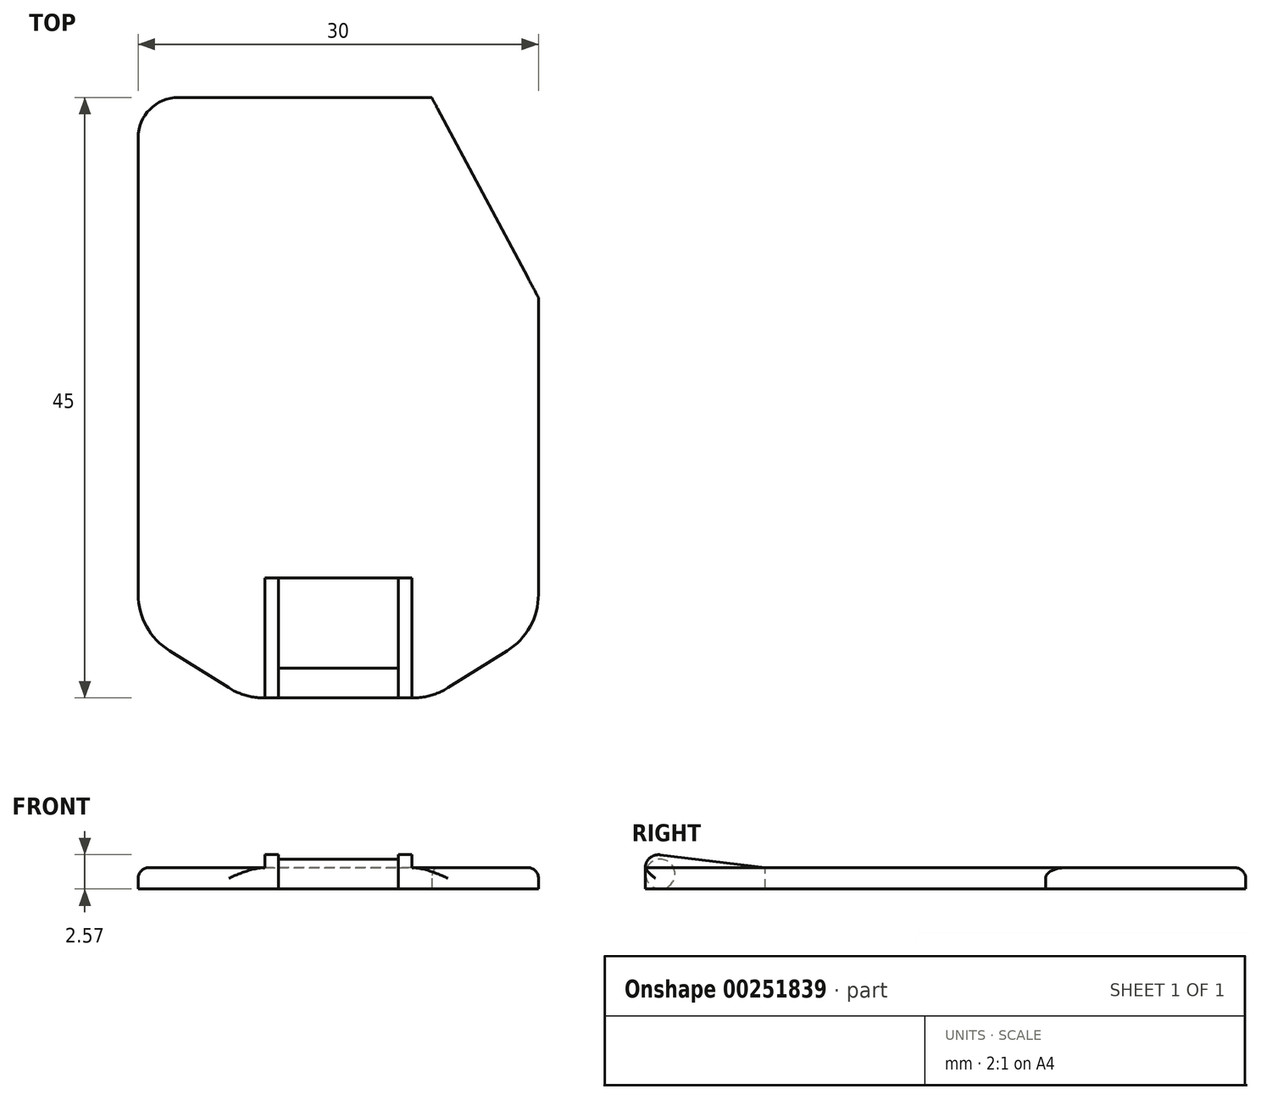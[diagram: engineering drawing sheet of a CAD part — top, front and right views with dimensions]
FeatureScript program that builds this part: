
annotation { "Feature Type Name" : "Feature", "Feature Type Description" : "" }
export const myFeature = defineFeature(function(context is Context, id is Id, definition is map)
    precondition{}
    {
        {
            var Q0;
            Q0=qCreatedBy(makeId("Top.planeOp"),FACE);
            var sketch = newSketch(context, id + "F0", { "sketchPlane" : qUnion([Q0])});
            skLineSegment(sketch, "E0.bottom", {"start": v(0, 0) * mm, "end": v(-30, 0) * mm});
            skLineSegment(sketch, "E0.top", {"start": v(0, 45) * mm, "end": v(-30, 45) * mm});
            skLineSegment(sketch, "E0.left", {"start": v(0, 0) * mm, "end": v(0, 45) * mm});
            skLineSegment(sketch, "E0.right", {"start": v(-30, 0) * mm, "end": v(-30, 45) * mm});
            skSolve(sketch);
        }
        {
            var Q0;
            Q0=makeQuery(id+"F0.imprint","IMPRINT",FACE,{"disambiguationData":[TD([[makeQuery(id+"F0.imprint","IMPRINT",EDGE,{"derivedFrom":sQuery(id+"F0.wireOp",EDGE,"E0.bottom")}),-1.0]])]});
            extrude(context, id + "F1", {"entities" : qUnion([Q0]), "depth" : 1.6 * mm});
        }
        {
            var Q0;
            Q0=makeQuery(id+"F1.opExtrude","SWEPT_EDGE",EDGE,{"disambiguationData":[OSD([sQuery(id+"F0.wireOp",EDGE,"E0.bottom"),sQuery(id+"F0.wireOp",EDGE,"E0.left")])]});
            var Q1;
            Q1=makeQuery(id+"F1.opExtrude","SWEPT_EDGE",EDGE,{"disambiguationData":[OSD([sQuery(id+"F0.wireOp",EDGE,"E0.bottom"),sQuery(id+"F0.wireOp",EDGE,"E0.right")])]});
            chamfer(context, id + "F2", {"entities" : qUnion([Q0, Q1]), "chamferType" : ChamferType.TWO_OFFSETS, "width1" : 5 * mm, "oppositeDirection" : false, "width2" : 8 * mm, "tangentPropagation" : true});
        }
        {
            var Q0;
            Q0=makeQuery(id+"F1.opExtrude","SWEPT_EDGE",EDGE,{"disambiguationData":[OSD([sQuery(id+"F0.wireOp",EDGE,"E0.top"),sQuery(id+"F0.wireOp",EDGE,"E0.left")])]});
            var Q1;
            Q1=makeQuery(id+"F1.opExtrude","SWEPT_EDGE",EDGE,{"disambiguationData":[OSD([sQuery(id+"F0.wireOp",EDGE,"E0.top"),sQuery(id+"F0.wireOp",EDGE,"E0.right")])]});
            fillet(context, id + "F3", {"entities" : qUnion([Q0, Q1]), "radius" : 3 * mm, "tangentPropagation" : true, "allowEdgeOverflow" : false});
        }
        {
            var Q0;
            Q0=makeQuery(id+"F13.boolean.opBoolean","MERGE",FACE,{"derivedFrom":[makeQuery(id+"F10.boolean.opBoolean","MERGE",FACE,{"derivedFrom":[makeQuery(id+"F1.opExtrude","CAP_FACE",FACE,{"disambiguationData":[OSD([sQuery(id+"F0.wireOp",EDGE,"E0.bottom"),sQuery(id+"F0.wireOp",EDGE,"E0.top"),sQuery(id+"F0.wireOp",EDGE,"E0.left"),sQuery(id+"F0.wireOp",EDGE,"E0.right")])],"isStart":true}),makeQuery(id+"F10.opExtrude","SWEPT_FACE",FACE,{"disambiguationData":[OSD([sQuery(id+"F9.wireOp",EDGE,"E8")])]})]}),makeQuery(id+"F13.opExtrude","SWEPT_FACE",FACE,{"disambiguationData":[OSD([sQuery(id+"F12.wireOp",EDGE,"E14")])]})]});
            var sketch = newSketch(context, id + "F4", { "sketchPlane" : qUnion([Q0])});
            skLineSegment(sketch, "E1", {"start": v(0, -30) * mm, "end": v(-8, -45) * mm});
            skLineSegment(sketch, "E2", {"start": v(-8, -45) * mm, "end": v(0, -45) * mm});
            skLineSegment(sketch, "E3", {"start": v(0, -45) * mm, "end": v(0, -30) * mm});
            skSolve(sketch);
        }
        {
            var Q0;
            Q0 = qSketchRegion(id + "F4", true);
            extrude(context, id + "F5", {"entities" : qUnion([Q0]), "operationType" : NewBodyOperationType.REMOVE, "oppositeDirection" : true, "depth" : 1.6 * mm});
        }
        {
            var Q0;
            Q0=makeQuery(id+"F1.opExtrude","CAP_FACE",FACE,{"disambiguationData":[OSD([sQuery(id+"F0.wireOp",EDGE,"E0.bottom"),sQuery(id+"F0.wireOp",EDGE,"E0.top"),sQuery(id+"F0.wireOp",EDGE,"E0.left"),sQuery(id+"F0.wireOp",EDGE,"E0.right")])],"isStart":false});
            var sketch = newSketch(context, id + "F6", { "sketchPlane" : qUnion([Q0])});
            skLineSegment(sketch, "E4", {"start": v(-22, 0) * mm, "end": v(-20.5, 0) * mm});
            skLineSegment(sketch, "E5", {"start": v(-8, 0) * mm, "end": v(-9.5, 0) * mm});
            skLineSegment(sketch, "E6.bottom", {"start": v(-20.5, 0) * mm, "end": v(-9.5, 0) * mm});
            skLineSegment(sketch, "E6.top", {"start": v(-20.5, 9) * mm, "end": v(-9.5, 9) * mm});
            skLineSegment(sketch, "E6.left", {"start": v(-20.5, 0) * mm, "end": v(-20.5, 9) * mm});
            skLineSegment(sketch, "E6.right", {"start": v(-9.5, 0) * mm, "end": v(-9.5, 9) * mm});
            skSolve(sketch);
        }
        {
            var Q0;
            Q0=makeQuery(id+"F6.imprint","IMPRINT",FACE,{"disambiguationData":[TD([[makeQuery(id+"F6.imprint","IMPRINT",EDGE,{"derivedFrom":sQuery(id+"F6.wireOp",EDGE,"E6.bottom")}),-1.0]])]});
            extrude(context, id + "F7", {"entities" : qUnion([Q0]), "operationType" : NewBodyOperationType.REMOVE, "oppositeDirection" : true, "depth" : 2 * mm});
        }
        {
            var Q0;
            {var subQ0=sQuery(id+"F0.wireOp",EDGE,"E0.left");Q0=makeQuery(id+"F2.opChamfer","BLEND_EDGE",EDGE,{"blendedFrom":[makeQuery(id+"F1.opExtrude","SWEPT_EDGE",EDGE,{"disambiguationData":[OSD([sQuery(id+"F0.wireOp",EDGE,"E0.bottom"),subQ0])]}),makeQuery(id+"F1.opExtrude","SWEPT_FACE",FACE,{"disambiguationData":[OSD([subQ0])]})],"blendedInto":[makeQuery(id+"F1.opExtrude","SWEPT_FACE",FACE,{"disambiguationData":[OSD([subQ0])]})]});}
            var Q1;
            {var subQ0=sQuery(id+"F0.wireOp",EDGE,"E0.bottom");Q1=makeQuery(id+"F2.opChamfer","BLEND_EDGE",EDGE,{"blendedFrom":[makeQuery(id+"F1.opExtrude","SWEPT_EDGE",EDGE,{"disambiguationData":[OSD([subQ0,sQuery(id+"F0.wireOp",EDGE,"E0.left")])]}),makeQuery(id+"F1.opExtrude","SWEPT_FACE",FACE,{"disambiguationData":[OSD([subQ0])]})],"blendedInto":[makeQuery(id+"F1.opExtrude","SWEPT_FACE",FACE,{"disambiguationData":[OSD([subQ0])]})]});}
            var Q2;
            {var subQ0=sQuery(id+"F0.wireOp",EDGE,"E0.bottom");Q2=makeQuery(id+"F2.opChamfer","BLEND_EDGE",EDGE,{"blendedFrom":[makeQuery(id+"F1.opExtrude","SWEPT_EDGE",EDGE,{"disambiguationData":[OSD([subQ0,sQuery(id+"F0.wireOp",EDGE,"E0.right")])]}),makeQuery(id+"F1.opExtrude","SWEPT_FACE",FACE,{"disambiguationData":[OSD([subQ0])]})],"blendedInto":[makeQuery(id+"F1.opExtrude","SWEPT_FACE",FACE,{"disambiguationData":[OSD([subQ0])]})]});}
            var Q3;
            {var subQ0=sQuery(id+"F0.wireOp",EDGE,"E0.right");Q3=makeQuery(id+"F2.opChamfer","BLEND_EDGE",EDGE,{"blendedFrom":[makeQuery(id+"F1.opExtrude","SWEPT_EDGE",EDGE,{"disambiguationData":[OSD([sQuery(id+"F0.wireOp",EDGE,"E0.bottom"),subQ0])]}),makeQuery(id+"F1.opExtrude","SWEPT_FACE",FACE,{"disambiguationData":[OSD([subQ0])]})],"blendedInto":[makeQuery(id+"F1.opExtrude","SWEPT_FACE",FACE,{"disambiguationData":[OSD([subQ0])]})]});}
            fillet(context, id + "F8", {"entities" : qUnion([Q0, Q1, Q2, Q3]), "radius" : 5 * mm, "tangentPropagation" : true, "allowEdgeOverflow" : false});
        }
        {
            var Q0;
            Q0=makeQuery(id+"F7.boolean.opBoolean","COPY",FACE,{"derivedFrom":makeQuery(id+"F7.opExtrude","SWEPT_FACE",FACE,{"disambiguationData":[OSD([sQuery(id+"F6.wireOp",EDGE,"E6.right")])]})});
            var sketch = newSketch(context, id + "F9", { "sketchPlane" : qUnion([Q0])});
            skLineSegment(sketch, "E7", {"start": v(-9, 1.6) * mm, "end": v(-9, 0) * mm});
            skLineSegment(sketch, "E8", {"start": v(-9, 0) * mm, "end": v(0, 0) * mm});
            skLineSegment(sketch, "E9", {"start": v(0, 0) * mm, "end": v(0, 2.7) * mm});
            skLineSegment(sketch, "E10", {"start": v(0, 2.7) * mm, "end": v(-9, 1.6) * mm});
            skSolve(sketch);
        }
        {
            var Q0;
            Q0=qSketchRegion(id+"F9",true);
            extrude(context, id + "F10", {"entities" : qUnion([Q0]), "operationType" : NewBodyOperationType.ADD, "depth" : 1 * mm});
        }
        {
            var Q0;
            Q0=makeQuery(id+"F10.opExtrude","SWEPT_EDGE",EDGE,{"disambiguationData":[OSD([sQuery(id+"F9.wireOp",EDGE,"E9"),sQuery(id+"F9.wireOp",EDGE,"E10")])]});
            fillet(context, id + "F11", {"entities" : qUnion([Q0]), "radius" : 1 * mm, "allowEdgeOverflow" : false});
        }
        {
            var Q0;
            Q0=makeQuery(id+"F7.boolean.opBoolean","COPY",FACE,{"derivedFrom":makeQuery(id+"F7.opExtrude","SWEPT_FACE",FACE,{"disambiguationData":[OSD([sQuery(id+"F6.wireOp",EDGE,"E6.left")])]})});
            var sketch = newSketch(context, id + "F12", { "sketchPlane" : qUnion([Q0])});
            skLineSegment(sketch, "E11", {"start": v(0, 0) * mm, "end": v(0, 2.7) * mm});
            skLineSegment(sketch, "E12", {"start": v(0, 2.7) * mm, "end": v(9, 1.6) * mm});
            skLineSegment(sketch, "E13", {"start": v(9, 1.6) * mm, "end": v(9, 0) * mm});
            skLineSegment(sketch, "E14", {"start": v(9, 0) * mm, "end": v(0, 0) * mm});
            skSolve(sketch);
        }
        {
            var Q0;
            Q0=qSketchRegion(id+"F12",true);
            extrude(context, id + "F13", {"entities" : qUnion([Q0]), "operationType" : NewBodyOperationType.ADD, "depth" : 1 * mm});
        }
        {
            var Q0;
            Q0=makeQuery(id+"F13.opExtrude","SWEPT_EDGE",EDGE,{"disambiguationData":[OSD([sQuery(id+"F12.wireOp",EDGE,"E11"),sQuery(id+"F12.wireOp",EDGE,"E12")])]});
            fillet(context, id + "F14", {"entities" : qUnion([Q0]), "radius" : 1 * mm, "tangentPropagation" : true, "allowEdgeOverflow" : false});
        }
        {
            var Q0;
            Q0=makeQuery(id+"F13.opExtrude","CAP_FACE",FACE,{"disambiguationData":[OSD([sQuery(id+"F12.wireOp",EDGE,"E11"),sQuery(id+"F12.wireOp",EDGE,"E12"),sQuery(id+"F12.wireOp",EDGE,"E13"),sQuery(id+"F12.wireOp",EDGE,"E14")])],"isStart":false});
            var sketch = newSketch(context, id + "F15", { "sketchPlane" : qUnion([Q0])});
            skLineSegment(sketch, "E15.bottom", {"start": v(0, 0) * mm, "end": v(2.25, 0) * mm});
            skLineSegment(sketch, "E15.top", {"start": v(0, 2.25) * mm, "end": v(2.25, 2.25) * mm});
            skLineSegment(sketch, "E15.left", {"start": v(0, 0) * mm, "end": v(0, 2.25) * mm});
            skLineSegment(sketch, "E15.right", {"start": v(2.25, 0) * mm, "end": v(2.25, 2.25) * mm});
            skCircle(sketch, "E16", {"center": v(1.13, 1.13) * mm, "radius": 1.1 * mm});
            skSolve(sketch);
        }
        {
            var Q0;
            Q0=makeQuery(id+"F1.opExtrude","CAP_EDGE",EDGE,{"disambiguationData":[OSD([sQuery(id+"F0.wireOp",EDGE,"E0.right")])],"isStart":false});
            var Q1;
            {var subQ0=sQuery(id+"F0.wireOp",EDGE,"E0.right");var subQ1=sQuery(id+"F0.wireOp",EDGE,"E0.bottom");Q1=makeQuery(id+"F2.opChamfer","BLEND_EDGE",EDGE,{"blendedFrom":[makeQuery(id+"F1.opExtrude","SWEPT_EDGE",EDGE,{"disambiguationData":[OSD([subQ1,subQ0])]}),makeQuery(id+"F1.opExtrude","CAP_FACE",FACE,{"disambiguationData":[OSD([subQ1,sQuery(id+"F0.wireOp",EDGE,"E0.top"),sQuery(id+"F0.wireOp",EDGE,"E0.left"),subQ0])],"isStart":false})],"blendedInto":[makeQuery(id+"F1.opExtrude","CAP_FACE",FACE,{"disambiguationData":[OSD([subQ1,sQuery(id+"F0.wireOp",EDGE,"E0.top"),sQuery(id+"F0.wireOp",EDGE,"E0.left"),subQ0])],"isStart":false})]});}
            var Q2;
            {var subQ0=sQuery(id+"F0.wireOp",EDGE,"E0.left");var subQ1=sQuery(id+"F0.wireOp",EDGE,"E0.bottom");Q2=makeQuery(id+"F2.opChamfer","BLEND_EDGE",EDGE,{"blendedFrom":[makeQuery(id+"F1.opExtrude","SWEPT_EDGE",EDGE,{"disambiguationData":[OSD([subQ1,subQ0])]}),makeQuery(id+"F1.opExtrude","CAP_FACE",FACE,{"disambiguationData":[OSD([subQ1,sQuery(id+"F0.wireOp",EDGE,"E0.top"),subQ0,sQuery(id+"F0.wireOp",EDGE,"E0.right")])],"isStart":false})],"blendedInto":[makeQuery(id+"F1.opExtrude","CAP_FACE",FACE,{"disambiguationData":[OSD([subQ1,sQuery(id+"F0.wireOp",EDGE,"E0.top"),subQ0,sQuery(id+"F0.wireOp",EDGE,"E0.right")])],"isStart":false})]});}
            var Q3;
            Q3=makeQuery(id+"F1.opExtrude","CAP_EDGE",EDGE,{"disambiguationData":[OSD([sQuery(id+"F0.wireOp",EDGE,"E0.left")])],"isStart":false});
            var Q4;
            {var subQ0=sQuery(id+"F0.wireOp",EDGE,"E0.left");var subQ1=sQuery(id+"F0.wireOp",EDGE,"E0.bottom");Q4=makeQuery(id+"F8.opFillet","BLEND_EDGE",EDGE,{"blendedFrom":[makeQuery(id+"F2.opChamfer","BLEND_EDGE",EDGE,{"blendedFrom":[makeQuery(id+"F1.opExtrude","SWEPT_EDGE",EDGE,{"disambiguationData":[OSD([subQ1,subQ0])]}),makeQuery(id+"F1.opExtrude","SWEPT_FACE",FACE,{"disambiguationData":[OSD([subQ0])]})],"blendedInto":[makeQuery(id+"F1.opExtrude","SWEPT_FACE",FACE,{"disambiguationData":[OSD([subQ0])]})]}),makeQuery(id+"F1.opExtrude","CAP_FACE",FACE,{"disambiguationData":[OSD([subQ1,sQuery(id+"F0.wireOp",EDGE,"E0.top"),subQ0,sQuery(id+"F0.wireOp",EDGE,"E0.right")])],"isStart":false})],"blendedInto":[makeQuery(id+"F1.opExtrude","CAP_FACE",FACE,{"disambiguationData":[OSD([subQ1,sQuery(id+"F0.wireOp",EDGE,"E0.top"),subQ0,sQuery(id+"F0.wireOp",EDGE,"E0.right")])],"isStart":false})]});}
            var Q5;
            {var subQ0=sQuery(id+"F0.wireOp",EDGE,"E0.right");var subQ1=sQuery(id+"F0.wireOp",EDGE,"E0.top");Q5=makeQuery(id+"F3.opFillet","BLEND_EDGE",EDGE,{"blendedFrom":[makeQuery(id+"F1.opExtrude","SWEPT_EDGE",EDGE,{"disambiguationData":[OSD([subQ1,subQ0])]}),makeQuery(id+"F1.opExtrude","CAP_FACE",FACE,{"disambiguationData":[OSD([sQuery(id+"F0.wireOp",EDGE,"E0.bottom"),subQ1,sQuery(id+"F0.wireOp",EDGE,"E0.left"),subQ0])],"isStart":false})],"blendedInto":[makeQuery(id+"F1.opExtrude","CAP_FACE",FACE,{"disambiguationData":[OSD([sQuery(id+"F0.wireOp",EDGE,"E0.bottom"),subQ1,sQuery(id+"F0.wireOp",EDGE,"E0.left"),subQ0])],"isStart":false})]});}
            var Q6;
            Q6=makeQuery(id+"F1.opExtrude","CAP_EDGE",EDGE,{"disambiguationData":[OSD([sQuery(id+"F0.wireOp",EDGE,"E0.top")])],"isStart":false});
            var Q7;
            {var subQ0=sQuery(id+"F0.wireOp",EDGE,"E0.left");var subQ1=sQuery(id+"F0.wireOp",EDGE,"E0.top");Q7=makeQuery(id+"F3.opFillet","BLEND_EDGE",EDGE,{"blendedFrom":[makeQuery(id+"F1.opExtrude","SWEPT_EDGE",EDGE,{"disambiguationData":[OSD([subQ1,subQ0])]}),makeQuery(id+"F1.opExtrude","CAP_FACE",FACE,{"disambiguationData":[OSD([sQuery(id+"F0.wireOp",EDGE,"E0.bottom"),subQ1,subQ0,sQuery(id+"F0.wireOp",EDGE,"E0.right")])],"isStart":false})],"blendedInto":[makeQuery(id+"F1.opExtrude","CAP_FACE",FACE,{"disambiguationData":[OSD([sQuery(id+"F0.wireOp",EDGE,"E0.bottom"),subQ1,subQ0,sQuery(id+"F0.wireOp",EDGE,"E0.right")])],"isStart":false})]});}
            var Q8;
            Q8=makeQuery(id+"F5.boolean.opBoolean","COPY",EDGE,{"derivedFrom":makeQuery(id+"F5.opExtrude","CAP_EDGE",EDGE,{"disambiguationData":[OSD([sQuery(id+"F4.wireOp",EDGE,"E1")])],"isStart":false})});
            fillet(context, id + "F16", {"entities" : qUnion([Q0, Q1, Q2, Q3, Q4, Q5, Q6, Q7, Q8]), "radius" : 0.8 * mm, "allowEdgeOverflow" : false});
        }
        {
            var Q0;
            Q0=makeQuery(id+"F15.imprint","IMPRINT",FACE,{"disambiguationData":[TD([[makeQuery(id+"F15.imprint","IMPRINT",EDGE,{"derivedFrom":sQuery(id+"F15.wireOp",EDGE,"E16")}),1.0]])]});
            extrude(context, id + "F17", {"entities" : qUnion([Q0]), "operationType" : NewBodyOperationType.ADD, "depth" : 9 * mm});
        }
    });
